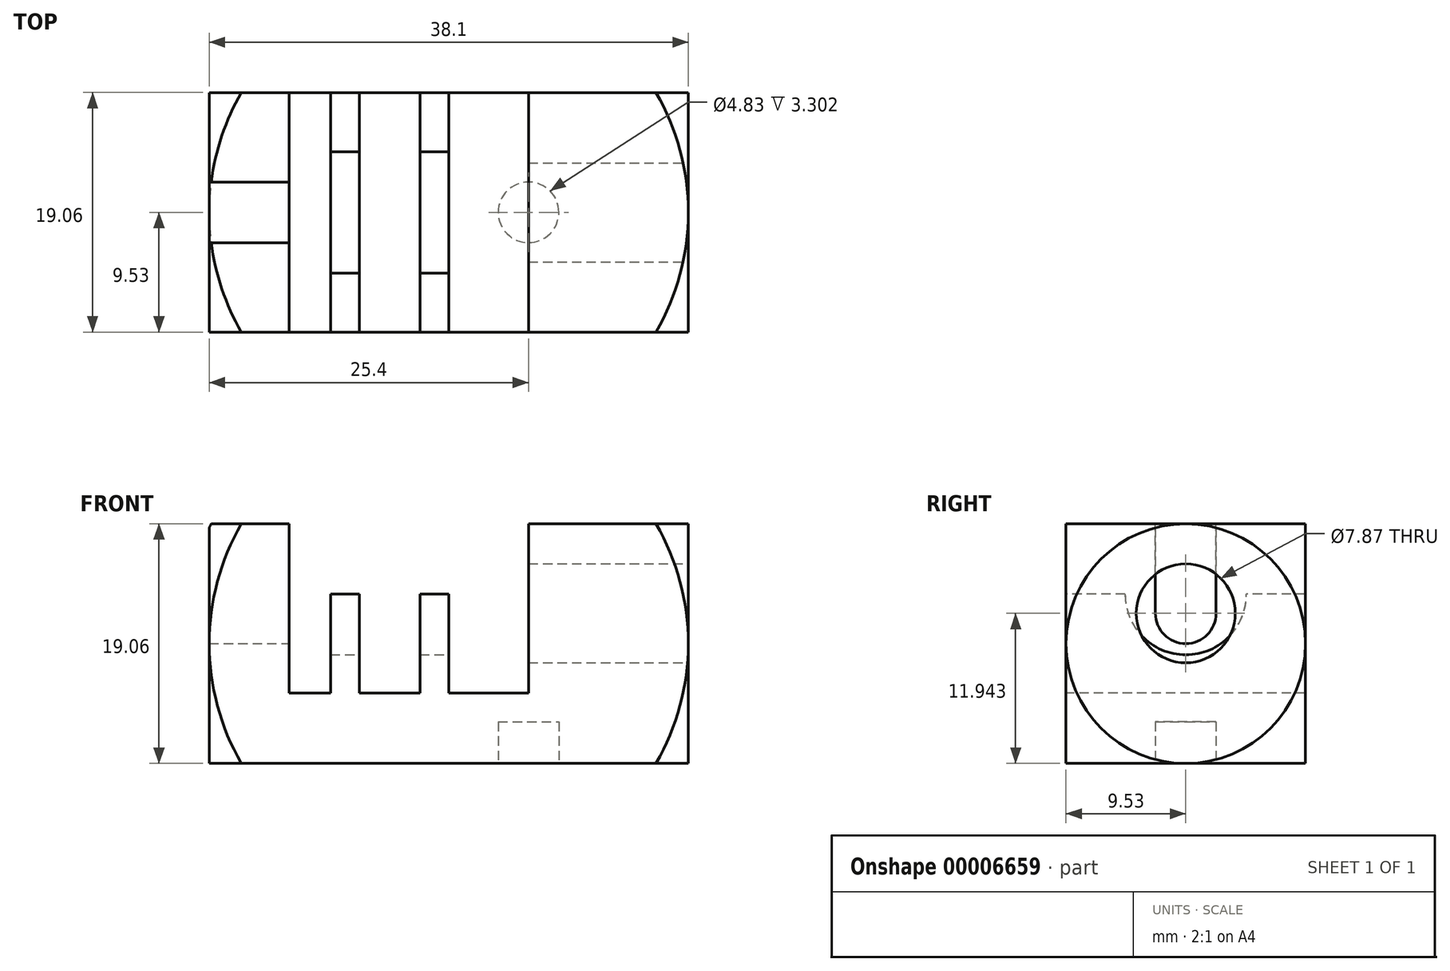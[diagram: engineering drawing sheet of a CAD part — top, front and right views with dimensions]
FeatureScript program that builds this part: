
annotation { "Feature Type Name" : "Feature", "Feature Type Description" : "" }
export const myFeature = defineFeature(function(context is Context, id is Id, definition is map)
    precondition{}
    {
        {
            var Q0;
            Q0=qCreatedBy(makeId("Front.planeOp"),FACE);
            var sketch = newSketch(context, id + "F0", { "sketchPlane" : qUnion([Q0])});
            skPoint(sketch, "E0.rect.middle", {"position": v(0, 0) * mm});
            skArc(sketch, "E1", {"start": v(21.3, 0) * mm, "mid": v(0, 21.3) * mm, "end": v(-21.3, 0) * mm});
            skLineSegment(sketch, "E2", {"start": v(-21.3, 0) * mm, "end": v(21.3, 0) * mm});
            skSolve(sketch);
        }
        {
            var Q0;
            Q0 = qSketchRegion(id + "F0", true);
            var Q1;
            Q1=sQuery(id+"F0.wireOp",EDGE,"E2");
            revolve(context, id + "F1", {"entities" : qUnion([Q0]), "axis" : qUnion([Q1]), "revolveType" : RevolveType.FULL});
        }
        {
            var Q0;
            Q0=qCreatedBy(makeId("Front.planeOp"),FACE);
            var sketch = newSketch(context, id + "F2", { "sketchPlane" : qUnion([Q0])});
            skLineSegment(sketch, "E3.rect.bottom", {"start": v(19.05, 9.53) * mm, "end": v(6.35, 9.53) * mm});
            skLineSegment(sketch, "E3.rect.top", {"start": v(19.05, -9.53) * mm, "end": v(-19.05, -9.53) * mm});
            skLineSegment(sketch, "E3.rect.left", {"start": v(19.05, 9.53) * mm, "end": v(19.05, -9.53) * mm});
            skLineSegment(sketch, "E3.rect.right", {"start": v(-19.05, 9.53) * mm, "end": v(-19.05, -9.53) * mm});
            skPoint(sketch, "E3.rect.middle", {"position": v(0, 0) * mm});
            skLineSegment(sketch, "E4", {"start": v(-12.7, 9.53) * mm, "end": v(-12.7, -3.94) * mm});
            skLineSegment(sketch, "E5", {"start": v(-12.7, -3.94) * mm, "end": v(-9.4, -3.94) * mm});
            skLineSegment(sketch, "E6", {"start": v(-9.4, -3.94) * mm, "end": v(-9.4, 3.94) * mm});
            skLineSegment(sketch, "E7", {"start": v(-9.4, 3.94) * mm, "end": v(-7.11, 3.94) * mm});
            skLineSegment(sketch, "E8", {"start": v(-7.11, 3.94) * mm, "end": v(-7.11, -3.94) * mm});
            skLineSegment(sketch, "E9", {"start": v(-7.11, -3.94) * mm, "end": v(-2.29, -3.94) * mm});
            skLineSegment(sketch, "E10", {"start": v(-2.29, -3.94) * mm, "end": v(-2.29, 3.94) * mm});
            skLineSegment(sketch, "E11", {"start": v(-2.29, 3.94) * mm, "end": v(0, 3.94) * mm});
            skLineSegment(sketch, "E12", {"start": v(0, 3.94) * mm, "end": v(0, -3.94) * mm});
            skLineSegment(sketch, "E13", {"start": v(0, -3.94) * mm, "end": v(6.35, -3.94) * mm});
            skLineSegment(sketch, "E14", {"start": v(6.35, -3.94) * mm, "end": v(6.35, 9.53) * mm});
            skLineSegment(sketch, "E15.trimOffspring", {"start": v(-12.7, 9.53) * mm, "end": v(-19.05, 9.53) * mm});
            skLineSegment(sketch, "E16.rect.bottom", {"start": v(57.36, 38.63) * mm, "end": v(-57.36, 38.63) * mm});
            skLineSegment(sketch, "E16.rect.top", {"start": v(57.36, -38.63) * mm, "end": v(-57.36, -38.63) * mm});
            skLineSegment(sketch, "E16.rect.left", {"start": v(57.36, 38.63) * mm, "end": v(57.36, -38.63) * mm});
            skLineSegment(sketch, "E16.rect.right", {"start": v(-57.36, 38.63) * mm, "end": v(-57.36, -38.63) * mm});
            skSolve(sketch);
        }
        {
            var Q0;
            Q0=makeQuery(id+"F2.imprint","IMPRINT",FACE,{"disambiguationData":[TD([[makeQuery(id+"F2.imprint","IMPRINT",EDGE,{"derivedFrom":sQuery(id+"F2.wireOp",EDGE,"E3.rect.bottom")}),-1.0]])]});
            extrude(context, id + "F3", {"entities" : qUnion([Q0]), "operationType" : NewBodyOperationType.REMOVE, "endBound" : BoundingType.SYMMETRIC, "oppositeDirection" : true, "depth" : 43.18 * mm});
        }
        {
            var Q0;
            Q0=qCreatedBy(makeId("Right.planeOp"),FACE);
            var sketch = newSketch(context, id + "F4", { "sketchPlane" : qUnion([Q0])});
            skLineSegment(sketch, "E17.rect.bottom", {"start": v(9.52, 9.53) * mm, "end": v(-9.53, 9.53) * mm});
            skLineSegment(sketch, "E17.rect.top", {"start": v(9.53, -9.53) * mm, "end": v(-9.52, -9.53) * mm});
            skLineSegment(sketch, "E17.rect.left", {"start": v(9.52, 9.53) * mm, "end": v(9.53, -9.53) * mm});
            skLineSegment(sketch, "E17.rect.right", {"start": v(-9.53, 9.53) * mm, "end": v(-9.52, -9.53) * mm});
            skPoint(sketch, "E17.rect.middle", {"position": v(0, 0) * mm});
            skLineSegment(sketch, "E18.rect.bottom", {"start": v(55.22, 39.52) * mm, "end": v(-55.22, 39.52) * mm});
            skLineSegment(sketch, "E18.rect.top", {"start": v(55.22, -39.52) * mm, "end": v(-55.22, -39.52) * mm});
            skLineSegment(sketch, "E18.rect.left", {"start": v(55.22, 39.52) * mm, "end": v(55.22, -39.52) * mm});
            skLineSegment(sketch, "E18.rect.right", {"start": v(-55.22, 39.52) * mm, "end": v(-55.22, -39.52) * mm});
            skSolve(sketch);
        }
        {
            var Q0;
            Q0 = qSketchRegion(id + "F4", true);
            extrude(context, id + "F5", {"entities" : qUnion([Q0]), "operationType" : NewBodyOperationType.REMOVE, "oppositeDirection" : true, "depth" : 25.4 * mm});
        }
        {
            var Q0;
            Q0 = qSketchRegion(id + "F4", true);
            extrude(context, id + "F6", {"entities" : qUnion([Q0]), "operationType" : NewBodyOperationType.REMOVE, "depth" : 25.4 * mm});
        }
        {
            var Q0;
            Q0=makeQuery(id+"F3.boolean.opBoolean","COPY",FACE,{"derivedFrom":makeQuery(id+"F3.opExtrude","SWEPT_FACE",FACE,{"disambiguationData":[OSD([sQuery(id+"F2.wireOp",EDGE,"E3.rect.left")])]})});
            var sketch = newSketch(context, id + "F7", { "sketchPlane" : qUnion([Q0])});
            skLineSegment(sketch, "E19", {"start": v(0, 0) * mm, "end": v(0, 2.41) * mm});
            skCircle(sketch, "E20", {"center": v(0, 2.41) * mm, "radius": 3.94 * mm});
            skSolve(sketch);
        }
        {
            var Q0;
            Q0 = qSketchRegion(id + "F7", true);
            extrude(context, id + "F8", {"entities" : qUnion([Q0]), "operationType" : NewBodyOperationType.REMOVE, "oppositeDirection" : true, "depth" : 12.7 * mm});
        }
        {
            var Q0;
            Q0=makeQuery(id+"F3.boolean.opBoolean","COPY",FACE,{"derivedFrom":makeQuery(id+"F3.opExtrude","SWEPT_FACE",FACE,{"disambiguationData":[OSD([sQuery(id+"F2.wireOp",EDGE,"E12")])]})});
            var sketch = newSketch(context, id + "F9", { "sketchPlane" : qUnion([Q0])});
            skCircle(sketch, "E21", {"center": v(0, 3.94) * mm, "radius": 4.83 * mm});
            skSolve(sketch);
        }
        {
            var Q0;
            Q0 = qSketchRegion(id + "F9", true);
            extrude(context, id + "F10", {"entities" : qUnion([Q0]), "operationType" : NewBodyOperationType.REMOVE, "oppositeDirection" : true, "depth" : 10.16 * mm});
        }
        {
            var Q0;
            Q0=makeQuery(id+"F3.boolean.opBoolean","COPY",FACE,{"derivedFrom":makeQuery(id+"F3.opExtrude","SWEPT_FACE",FACE,{"disambiguationData":[OSD([sQuery(id+"F2.wireOp",EDGE,"E4")])]})});
            var sketch = newSketch(context, id + "F11", { "sketchPlane" : qUnion([Q0])});
            skArc(sketch, "E22", {"start": v(-2.41, 2.41) * mm, "mid": v(0, 0) * mm, "end": v(2.41, 2.41) * mm});
            skLineSegment(sketch, "E23", {"start": v(-2.41, 2.41) * mm, "end": v(-2.41, 9.53) * mm});
            skLineSegment(sketch, "E24", {"start": v(2.41, 2.41) * mm, "end": v(2.41, 9.53) * mm});
            skLineSegment(sketch, "E25", {"start": v(2.41, 9.53) * mm, "end": v(-2.41, 9.53) * mm});
            skSolve(sketch);
        }
        {
            var Q0;
            Q0 = qSketchRegion(id + "F11", true);
            extrude(context, id + "F12", {"entities" : qUnion([Q0]), "operationType" : NewBodyOperationType.REMOVE, "oppositeDirection" : true, "depth" : 25.4 * mm});
        }
        {
            var Q0;
            Q0=makeQuery(id+"F3.boolean.opBoolean","COPY",FACE,{"derivedFrom":makeQuery(id+"F3.opExtrude","SWEPT_FACE",FACE,{"disambiguationData":[OSD([sQuery(id+"F2.wireOp",EDGE,"E3.rect.top")])]})});
            var sketch = newSketch(context, id + "F13", { "sketchPlane" : qUnion([Q0])});
            skLineSegment(sketch, "E26", {"start": v(19.05, 0) * mm, "end": v(6.35, 0) * mm});
            skCircle(sketch, "E27", {"center": v(6.35, 0) * mm, "radius": 2.41 * mm});
            skSolve(sketch);
        }
        {
            var Q0;
            Q0 = qSketchRegion(id + "F13", true);
            extrude(context, id + "F14", {"entities" : qUnion([Q0]), "operationType" : NewBodyOperationType.REMOVE, "oppositeDirection" : true, "depth" : 3.3 * mm});
        }
    });
